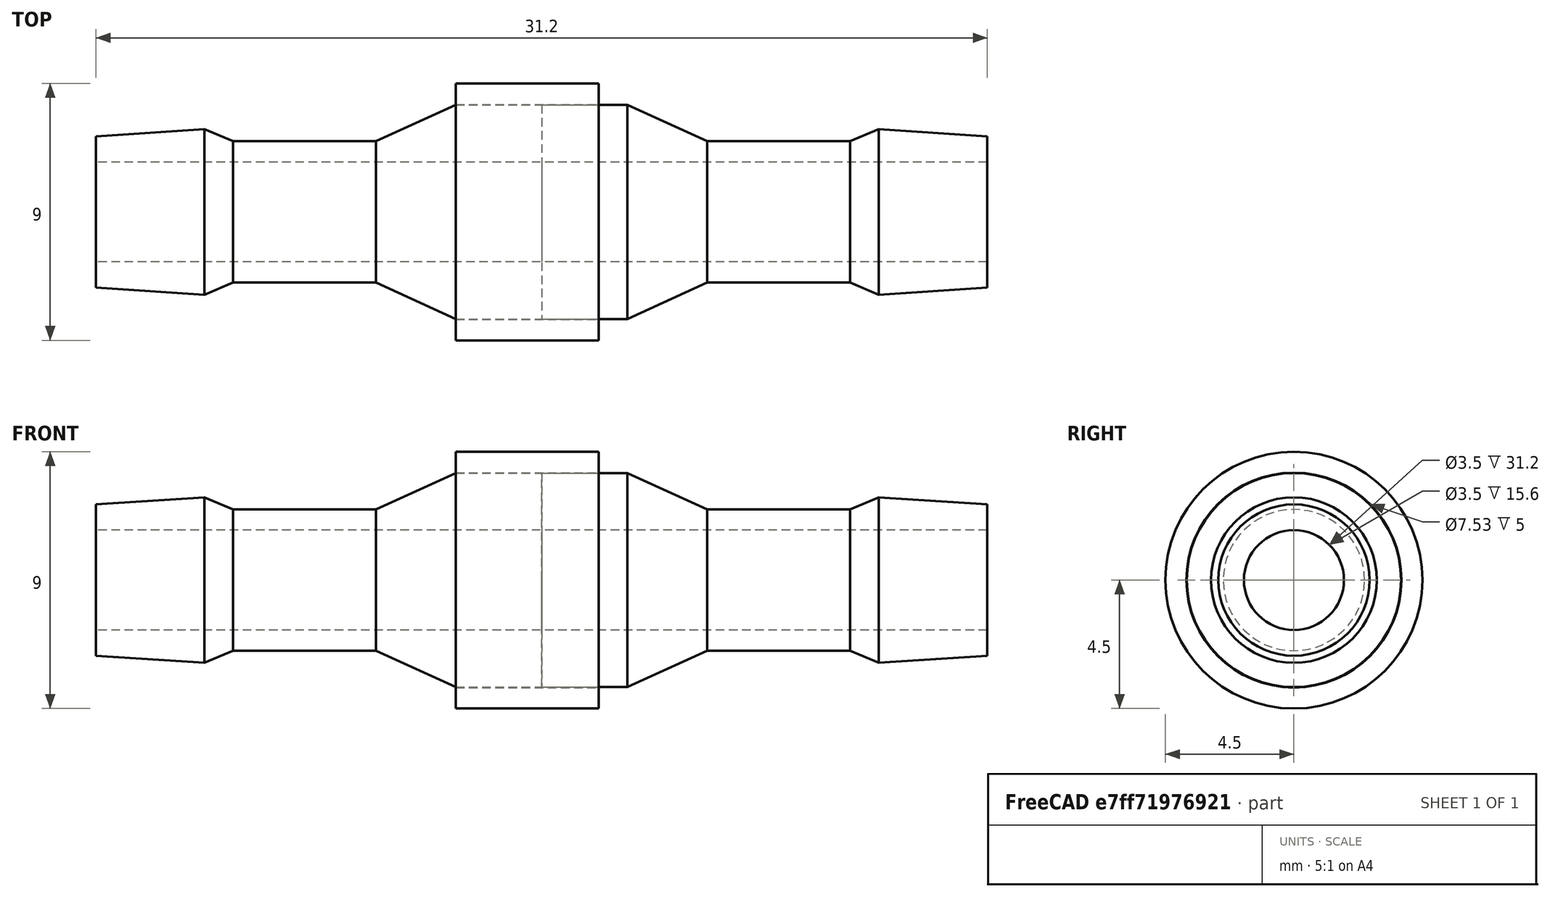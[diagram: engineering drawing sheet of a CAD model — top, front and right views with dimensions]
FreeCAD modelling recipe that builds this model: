
FCSTD DOCUMENT  (FreeCAD 0.19R24276 (Git))
Label: empalme_tubo_limpiaparabrisas
License: All rights reserved
LicenseURL: http://en.wikipedia.org/wiki/All_rights_reserved
objects: Mesh::Feature×3, Sketcher::SketchObject×2, PartDesign::Revolution×2, PartDesign::Body×2, Part::Cylinder×2, PartDesign::Mirrored×1, Part::Cut×1
note: 12 computed .brp shape members not serialized (recipe doc carries the construction recipe); baked Part::Feature solids carry a one-line shape summary decoded from their .brp

FEATURE [Sketcher::SketchObject] Sketch
  FullyConstrained = true
  MapMode = 5
  Support = -> [XY_Plane]
  sketch-geometry (8):
    g0: LineSegment StartX=0 StartY=1.75 StartZ=0 EndX=0 EndY=3.75 EndZ=0
    g1: LineSegment StartX=0 StartY=3.75 StartZ=0 EndX=3 EndY=3.75 EndZ=0
    g2: LineSegment StartX=3 StartY=3.75 StartZ=0 EndX=5.8 EndY=2.475 EndZ=0
    g3: LineSegment StartX=5.8 StartY=2.475 StartZ=0 EndX=10.8 EndY=2.475 EndZ=0
    g4: LineSegment StartX=10.8 StartY=2.475 StartZ=0 EndX=11.8 EndY=2.9 EndZ=0
    g5: LineSegment StartX=11.8 StartY=2.9 StartZ=0 EndX=15.6 EndY=2.65 EndZ=0
    g6: LineSegment StartX=15.6 StartY=2.65 StartZ=0 EndX=15.6 EndY=1.75 EndZ=0
    g7: LineSegment StartX=15.6 StartY=1.75 StartZ=0 EndX=0 EndY=1.75 EndZ=0
  constraints (24):
    c: Vertical(g0)
    c: Coincident(g0,g1)
    c: Horizontal(g1)
    c: Coincident(g1,g2)
    c: Coincident(g2,g3)
    c: Horizontal(g3)
    c: Coincident(g3,g4)
    c: Coincident(g4,g5)
    c: Coincident(g5,g6)
    c: Vertical(g6)
    c: Coincident(g6,g7)
    c: Coincident(g7,g0)
    c: Horizontal(g7)
    c: PointOnObject(g0,g-2)
    c: DistanceY(g-1,g0) = 3.75
    c: DistanceY(g-1,g0) = 1.75
    c: DistanceX(g0,g1) = 3
    c: DistanceY(g-1,g2) = 2.475
    c: DistanceX(g1,g2) = 2.8
    c: DistanceX(g2,g3) = 5
    c: DistanceX(g3,g4) = 1
    c: DistanceX(g4,g5) = 3.8
    c: DistanceY(g-1,g5) = 2.65
    c: DistanceY(g-1,g4) = 2.9
FEATURE [PartDesign::Revolution] Revolution
  Angle = 360
  Axis = (1,0,0)
  Base = (0,0,0)
  Profile = -> Sketch
  ReferenceAxis = -> Sketch [H_Axis]
  Refine = true
FEATURE [PartDesign::Mirrored] Mirrored
  BaseFeature = -> Revolution
  MirrorPlane = -> Sketch [V_Axis]
  Originals = -> [Revolution]
  Refine = true
FEATURE [PartDesign::Body] Body  label="tubo001"
  Group = -> [Sketch,Revolution,Mirrored]
  Origin = -> Origin
  Tip = -> Mirrored
FEATURE [Mesh::Feature] Mesh  label="tubo"
FEATURE [Sketcher::SketchObject] Sketch001
  FullyConstrained = true
  MapMode = 5
  Support = -> [XY_Plane001]
  sketch-geometry (8):
    g0: LineSegment StartX=0 StartY=1.75 StartZ=0 EndX=0 EndY=3.75 EndZ=0
    g1: LineSegment StartX=0 StartY=3.75 StartZ=0 EndX=3 EndY=3.75 EndZ=0
    g2: LineSegment StartX=3 StartY=3.75 StartZ=0 EndX=5.8 EndY=2.475 EndZ=0
    g3: LineSegment StartX=5.8 StartY=2.475 StartZ=0 EndX=10.8 EndY=2.475 EndZ=0
    g4: LineSegment StartX=10.8 StartY=2.475 StartZ=0 EndX=11.8 EndY=2.9 EndZ=0
    g5: LineSegment StartX=11.8 StartY=2.9 StartZ=0 EndX=15.6 EndY=2.65 EndZ=0
    g6: LineSegment StartX=15.6 StartY=2.65 StartZ=0 EndX=15.6 EndY=1.75 EndZ=0
    g7: LineSegment StartX=15.6 StartY=1.75 StartZ=0 EndX=0 EndY=1.75 EndZ=0
  constraints (24):
    c: Vertical(g0)
    c: Coincident(g0,g1)
    c: Horizontal(g1)
    c: Coincident(g1,g2)
    c: Coincident(g2,g3)
    c: Horizontal(g3)
    c: Coincident(g3,g4)
    c: Coincident(g4,g5)
    c: Coincident(g5,g6)
    c: Vertical(g6)
    c: Coincident(g6,g7)
    c: Coincident(g7,g0)
    c: Horizontal(g7)
    c: PointOnObject(g0,g-2)
    c: DistanceY(g-1,g0) = 3.75
    c: DistanceY(g-1,g0) = 1.75
    c: DistanceX(g0,g1) = 3
    c: DistanceY(g-1,g2) = 2.475
    c: DistanceX(g1,g2) = 2.8
    c: DistanceX(g2,g3) = 5
    c: DistanceX(g3,g4) = 1
    c: DistanceX(g4,g5) = 3.8
    c: DistanceY(g-1,g5) = 2.65
    c: DistanceY(g-1,g4) = 2.9
FEATURE [PartDesign::Revolution] Revolution001
  Angle = 360
  Axis = (1,0,0)
  Base = (0,0,0)
  Profile = -> Sketch001
  ReferenceAxis = -> Sketch001 [H_Axis]
  Refine = true
FEATURE [PartDesign::Body] Body001  label="medio_tubo001"
  Group = -> [Sketch001,Revolution001]
  Origin = -> Origin001
  Tip = -> Revolution001
FEATURE [Mesh::Feature] Mesh001  label="medio_tubo"
FEATURE [Part::Cylinder] Cylinder
  Angle = 360
  AttacherType = Attacher::AttachEngine3D
  Height = 5
  Placement = pos=(0,0,10) rot=(0,0,1;0rad)
  Radius = 3.765
FEATURE [Part::Cylinder] Cylinder001
  Angle = 360
  AttacherType = Attacher::AttachEngine3D
  Height = 5
  Placement = pos=(0,0,10) rot=(0,0,1;0rad)
  Radius = 4.5
FEATURE [Part::Cut] Cut  label="empalme"
  Base = -> Cylinder001
  Placement = pos=(-13,0,0) rot=(0,1,0;1.5708rad)
  Refine = true
  Tool = -> Cylinder
FEATURE [Mesh::Feature] Mesh002  label="empalme (Meshed)"
